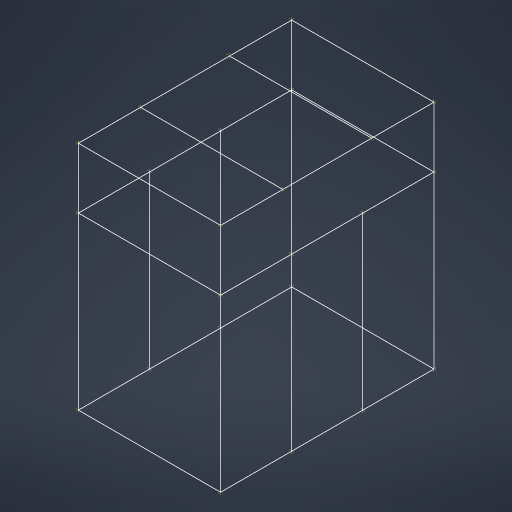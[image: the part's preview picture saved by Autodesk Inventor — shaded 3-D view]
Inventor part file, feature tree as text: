
AUTODESK INVENTOR PART (.ipt)
format: ipt  version: 2024.1 (Build 281209000, 209)  size: 198,144 bytes
history: native  units: mm
features: sketch x11, plane x4
ambient origin geometry x8: Origin, YZ Plane, XZ Plane, XY Plane, X Axis, Y Axis, Z Axis, Center Point
feature tree (15):
  sketch  "Sketch1"  dims[d0=800.0mm]
  sketch  "3D Sketch1"
  plane  "Work Plane1"
  sketch  "Sketch2"  dims[d1=1200.0mm]
  sketch  "3D Sketch2"
  sketch  "3D Sketch4"
  plane  "Work Plane2"
  sketch  "Sketch3"  dims[d2=0.0mm]
  sketch  "3D Sketch5"
  plane  "Work Plane3"
  sketch  "Sketch4"  dims[d3=1300.0mm]
  sketch  "3D Sketch6"
  plane  "Work Plane4"
  sketch  "Sketch5"  dims[d4=500.0mm d5=-340.0mm d6=400.0mm]
  sketch  "3D Sketch7"
